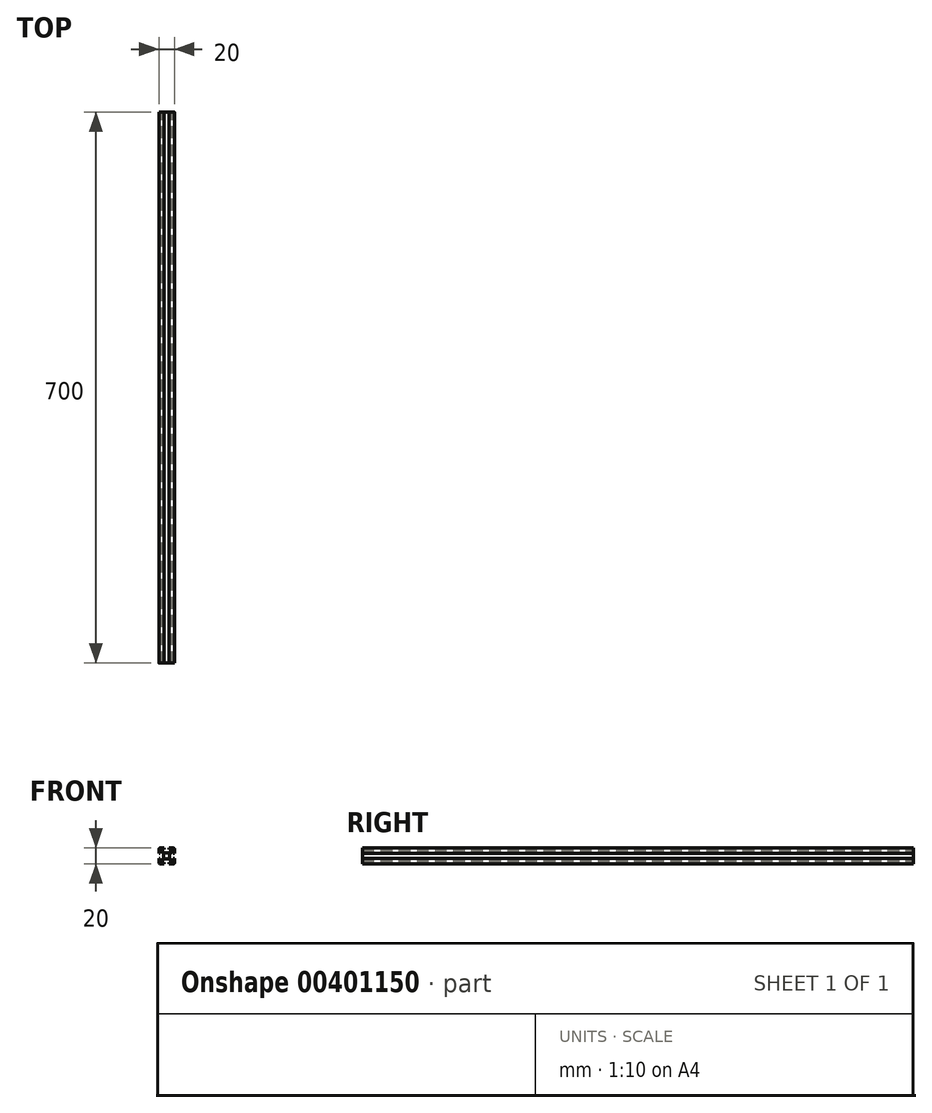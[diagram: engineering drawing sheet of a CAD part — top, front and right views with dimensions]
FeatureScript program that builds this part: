
annotation { "Feature Type Name" : "Feature", "Feature Type Description" : "" }
export const myFeature = defineFeature(function(context is Context, id is Id, definition is map)
    precondition{}
    {
        {
            var Q0;
            Q0=qCreatedBy(makeId("Front.planeOp"),FACE);
            var sketch = newSketch(context, id + "F0", { "sketchPlane" : qUnion([Q0])});
            skLineSegment(sketch, "E0.bottom", {"start": v(10, 10) * mm, "end": v(-10, 10) * mm});
            skLineSegment(sketch, "E0.top", {"start": v(10, -10) * mm, "end": v(-10, -10) * mm});
            skLineSegment(sketch, "E0.left", {"start": v(10, 10) * mm, "end": v(10, -10) * mm});
            skLineSegment(sketch, "E0.right", {"start": v(-10, 10) * mm, "end": v(-10, -10) * mm});
            skPoint(sketch, "E0.middle", {"position": v(0, 0) * mm});
            skLineSegment(sketch, "E1", {"start": v(3.11, 10) * mm, "end": v(3.11, 8.22) * mm});
            skLineSegment(sketch, "E2", {"start": v(3.11, 8.22) * mm, "end": v(5.46, 8.22) * mm});
            skLineSegment(sketch, "E3", {"start": v(5.46, 8.22) * mm, "end": v(5.46, 6.44) * mm});
            skLineSegment(sketch, "E4", {"start": v(5.46, 6.44) * mm, "end": v(3.11, 3.78) * mm});
            skLineSegment(sketch, "E5", {"start": v(3.11, 3.78) * mm, "end": v(0, 3.78) * mm});
            skLineSegment(sketch, "E6.MirrorCS", {"start": v(-3.11, 3.78) * mm, "end": v(0, 3.78) * mm});
            skLineSegment(sketch, "E7.MirrorCS", {"start": v(-5.46, 6.44) * mm, "end": v(-3.11, 3.78) * mm});
            skLineSegment(sketch, "E8.MirrorCS", {"start": v(-3.11, 10) * mm, "end": v(-3.11, 8.22) * mm});
            skLineSegment(sketch, "E9.MirrorCS", {"start": v(-5.46, 8.22) * mm, "end": v(-5.46, 6.44) * mm});
            skLineSegment(sketch, "E10.MirrorCS", {"start": v(-3.11, 8.22) * mm, "end": v(-5.46, 8.22) * mm});
            skLineSegment(sketch, "E11.1.0", {"start": v(-10, 3.11) * mm, "end": v(-8.22, 3.11) * mm});
            skLineSegment(sketch, "E11.1.1", {"start": v(-8.22, 3.11) * mm, "end": v(-8.22, 5.46) * mm});
            skLineSegment(sketch, "E11.1.2", {"start": v(-8.22, 5.46) * mm, "end": v(-6.44, 5.46) * mm});
            skLineSegment(sketch, "E11.1.3", {"start": v(-6.44, 5.46) * mm, "end": v(-3.78, 3.11) * mm});
            skLineSegment(sketch, "E11.1.4", {"start": v(-3.78, 3.11) * mm, "end": v(-3.78, 0) * mm});
            skLineSegment(sketch, "E11.1.5", {"start": v(-3.78, -3.11) * mm, "end": v(-3.78, 0) * mm});
            skLineSegment(sketch, "E11.1.6", {"start": v(-6.44, -5.46) * mm, "end": v(-3.78, -3.11) * mm});
            skLineSegment(sketch, "E11.1.7", {"start": v(-10, -3.11) * mm, "end": v(-8.22, -3.11) * mm});
            skLineSegment(sketch, "E11.1.8", {"start": v(-8.22, -5.46) * mm, "end": v(-6.44, -5.46) * mm});
            skLineSegment(sketch, "E11.1.9", {"start": v(-8.22, -3.11) * mm, "end": v(-8.22, -5.46) * mm});
            skLineSegment(sketch, "E11.2.0", {"start": v(-3.11, -10) * mm, "end": v(-3.11, -8.22) * mm});
            skLineSegment(sketch, "E11.2.1", {"start": v(-3.11, -8.22) * mm, "end": v(-5.46, -8.22) * mm});
            skLineSegment(sketch, "E11.2.2", {"start": v(-5.46, -8.22) * mm, "end": v(-5.46, -6.44) * mm});
            skLineSegment(sketch, "E11.2.3", {"start": v(-5.46, -6.44) * mm, "end": v(-3.11, -3.78) * mm});
            skLineSegment(sketch, "E11.2.4", {"start": v(-3.11, -3.78) * mm, "end": v(0, -3.78) * mm});
            skLineSegment(sketch, "E11.2.5", {"start": v(3.11, -3.78) * mm, "end": v(0, -3.78) * mm});
            skLineSegment(sketch, "E11.2.6", {"start": v(5.46, -6.44) * mm, "end": v(3.11, -3.78) * mm});
            skLineSegment(sketch, "E11.2.7", {"start": v(3.11, -10) * mm, "end": v(3.11, -8.22) * mm});
            skLineSegment(sketch, "E11.2.8", {"start": v(5.46, -8.22) * mm, "end": v(5.46, -6.44) * mm});
            skLineSegment(sketch, "E11.2.9", {"start": v(3.11, -8.22) * mm, "end": v(5.46, -8.22) * mm});
            skLineSegment(sketch, "E11.3.0", {"start": v(10, -3.11) * mm, "end": v(8.22, -3.11) * mm});
            skLineSegment(sketch, "E11.3.1", {"start": v(8.22, -3.11) * mm, "end": v(8.22, -5.46) * mm});
            skLineSegment(sketch, "E11.3.2", {"start": v(8.22, -5.46) * mm, "end": v(6.44, -5.46) * mm});
            skLineSegment(sketch, "E11.3.3", {"start": v(6.44, -5.46) * mm, "end": v(3.78, -3.11) * mm});
            skLineSegment(sketch, "E11.3.4", {"start": v(3.78, -3.11) * mm, "end": v(3.78, 0) * mm});
            skLineSegment(sketch, "E11.3.5", {"start": v(3.78, 3.11) * mm, "end": v(3.78, 0) * mm});
            skLineSegment(sketch, "E11.3.6", {"start": v(6.44, 5.46) * mm, "end": v(3.78, 3.11) * mm});
            skLineSegment(sketch, "E11.3.7", {"start": v(10, 3.11) * mm, "end": v(8.22, 3.11) * mm});
            skLineSegment(sketch, "E11.3.8", {"start": v(8.22, 5.46) * mm, "end": v(6.44, 5.46) * mm});
            skLineSegment(sketch, "E11.3.9", {"start": v(8.22, 3.11) * mm, "end": v(8.22, 5.46) * mm});
            skSolve(sketch);
        }
        {
            var Q0;
            {var subQ12=sQuery(id+"F0.wireOp",EDGE,"E1");Q0=makeQuery(id+"F0.imprint","IMPRINT",FACE,{"disambiguationData":[TD([[makeQuery(id+"F0.imprint","IMPRINT",EDGE,{"derivedFrom":subQ12}),1.0]])]});}
            extrude(context, id + "F1", {"entities" : qUnion([Q0]), "endBound" : BoundingType.SYMMETRIC, "depth" : 700 * mm});
        }
        {
            var Q0;
            Q0=makeQuery(id+"F1.opExtrude","SWEPT_EDGE",EDGE,{"disambiguationData":[OSD([sQuery(id+"F0.wireOp",EDGE,"E0.bottom"),sQuery(id+"F0.wireOp",EDGE,"E0.right")])]});
            var Q1;
            Q1=makeQuery(id+"F1.opExtrude","SWEPT_EDGE",EDGE,{"disambiguationData":[OSD([sQuery(id+"F0.wireOp",EDGE,"E0.bottom"),sQuery(id+"F0.wireOp",EDGE,"E0.left")])]});
            var Q2;
            Q2=makeQuery(id+"F1.opExtrude","SWEPT_EDGE",EDGE,{"disambiguationData":[OSD([sQuery(id+"F0.wireOp",EDGE,"E0.top"),sQuery(id+"F0.wireOp",EDGE,"E0.left")])]});
            var Q3;
            Q3=makeQuery(id+"F1.opExtrude","SWEPT_EDGE",EDGE,{"disambiguationData":[OSD([sQuery(id+"F0.wireOp",EDGE,"E0.top"),sQuery(id+"F0.wireOp",EDGE,"E0.right")])]});
            fillet(context, id + "F2", {"entities" : qUnion([Q0, Q1, Q2, Q3]), "radius" : 1.5 * mm, "tangentPropagation" : true, "allowEdgeOverflow" : false});
        }
    });
